# Revit family: Pressure independent control valve 4006_M
name_source: partatom
category: Rohrzubehör
revit_build: Autodesk Revit 2018 (Build: 20190510_1515(x64)
units: mm (PartAtom-declared; Revit-internal decimal feet)

## family parameters
Arbeitsebenenbasiert = Nein
Beim Laden mit Abzugskörper schneiden = Nein
Bemaßung runder Anschluss = Durchmesser verwenden
Gemeinsam genutzt = Nein
Immer vertikal = Ja
OmniClass-Nummer = 23.65.55.14
OmniClass-Titel = Valves for Liquid Services
Teiletyp = Unterbricht

## types (1)
- Pressure independent control valve 4006_M
    Application = the Pressure Independent Balancing Control Valve (PIBCV) is used in all heating and cooling systems with circulation pumps.
the valve automatically maintains flow to the required part of the system at the set rate by measuring and immediately adjusting to any variation in pressure.
no additional measurements are necessary and the correct flow rate is achieved at all operating conditions.
the diaphragm responds to the pressure upstream and downstream of the regulating valve (via an internal impulse line).
the valve settings directly affect the volumetric flow through the valve.
it is thus possible to set the maximum flow rate based on the flow chart when the valve is fitted.
this allows for the balancing of heating circuits, cooling water systems, ceiling cooling and heating panels, air heaters, etc. without any need to first assess the pressure variations in the system.
the valve‘s principal application is as a control valve for terminal units.
    Capillary pipe = copper Cu-DHP (CW024A)
    H05 = 9 mm  [stored 0.0295276 ft]
    H07 = 4 mm  [stored 0.0131234 ft]
    H09 = 21.8 mm  [stored 0.0715223 ft]
    H12 = 19.25 mm  [stored 0.0631562 ft]
    Hersteller = Herz-Armaturen GmbH
    Housing = DZR brass CC770S
    L02 = 43.5 mm  [stored 0.142717 ft]
    L03 = 3.2 mm  [stored 0.0104987 ft]
    L04 = 1.5 mm  [stored 0.00492126 ft]
    L05 = 11 mm  [stored 0.0360892 ft]
    Medium = water purity in accordance with the ÖNORM H5195 and VDI 2035 standards
ethylene and propylene glycol in a mixture ratio of 25 - 50% by volume [%] is permitted.
    Membrane = EPDM
    Membrane housing = brass CW602N
    O-Rings = EPDM
    PN = 16
    Pin = stainless steel 14301
    Protective cap = plastic
    R04 = 12.5 mm  [stored 0.0410105 ft]
    R05 = 15 mm  [stored 0.0492126 ft]
    R08 = 11.3 mm  [stored 0.0370735 ft]
    R09 = 18.25 mm  [stored 0.0598753 ft]
    R10 = 35 mm  [stored 0.114829 ft]
    R11 = 6.5 mm
    R12 = 3.9 mm  [stored 0.0127953 ft]
    SCRNCODE = 05;04;02
    SCRNSEQ = ARM;ARM_TYP="DURR";2
    Spring = spring steel
    Stroke = 4 mm  [stored 0.0131234 ft]
    URL = www.herzvalves.com
    VRL02 = 18 mm  [stored 0.0590551 ft]
    VRL04 = 8 mm  [stored 0.0262467 ft]
    max. Operating pressure = 1600000.0 Pa
    max. Operating temperature from DN40 = 110 °C
    max. Operating temperature till DN32 = 130 °C
    min. Operating temperature (antifreeze) = -20 °C
    min. Operating temperature (pure water) = 2 °C

note: [stored X ft] marks values corroborated as IEEE doubles in the binary element streams (Revit-internal decimal feet)
